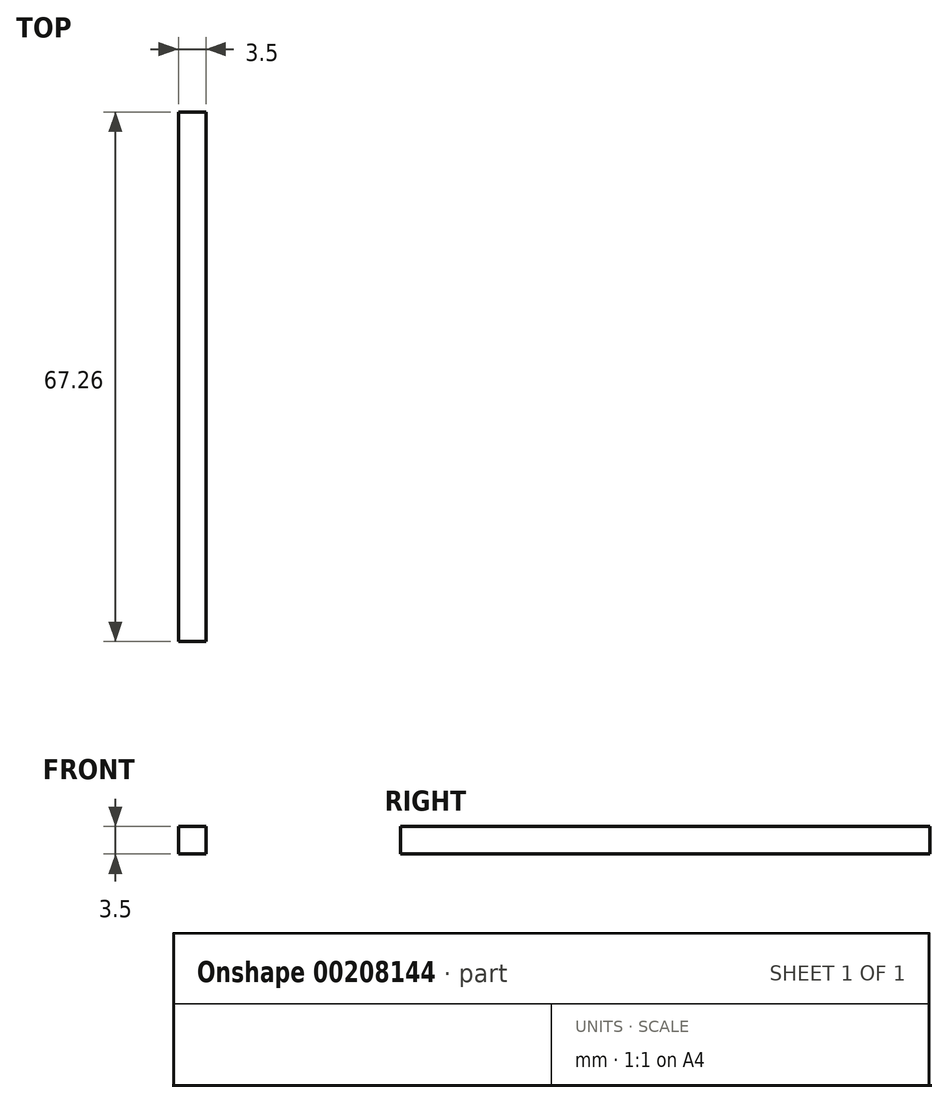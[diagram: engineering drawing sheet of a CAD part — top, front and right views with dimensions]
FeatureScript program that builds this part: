
annotation { "Feature Type Name" : "Feature", "Feature Type Description" : "" }
export const myFeature = defineFeature(function(context is Context, id is Id, definition is map)
    precondition{}
    {
        {
            var Q0;
            Q0=qCreatedBy(makeId("Top.planeOp"),FACE);
            var sketch = newSketch(context, id + "F0", { "sketchPlane" : qUnion([Q0])});
            skLineSegment(sketch, "E0.bottom", {"start": v(1.75, -33.64) * mm, "end": v(-1.75, -33.64) * mm});
            skLineSegment(sketch, "E0.top", {"start": v(1.75, 33.64) * mm, "end": v(-1.75, 33.64) * mm});
            skLineSegment(sketch, "E0.left", {"start": v(1.75, -33.64) * mm, "end": v(1.75, 33.63) * mm});
            skLineSegment(sketch, "E0.right", {"start": v(-1.75, -33.64) * mm, "end": v(-1.75, 33.63) * mm});
            skPoint(sketch, "E0.middle", {"position": v(0, 0) * mm});
            skSolve(sketch);
        }
        {
            var Q0;
            Q0 = qSketchRegion(id + "F0", true);
            extrude(context, id + "F1", {"entities" : qUnion([Q0]), "depth" : 3.5 * mm});
        }
    });
